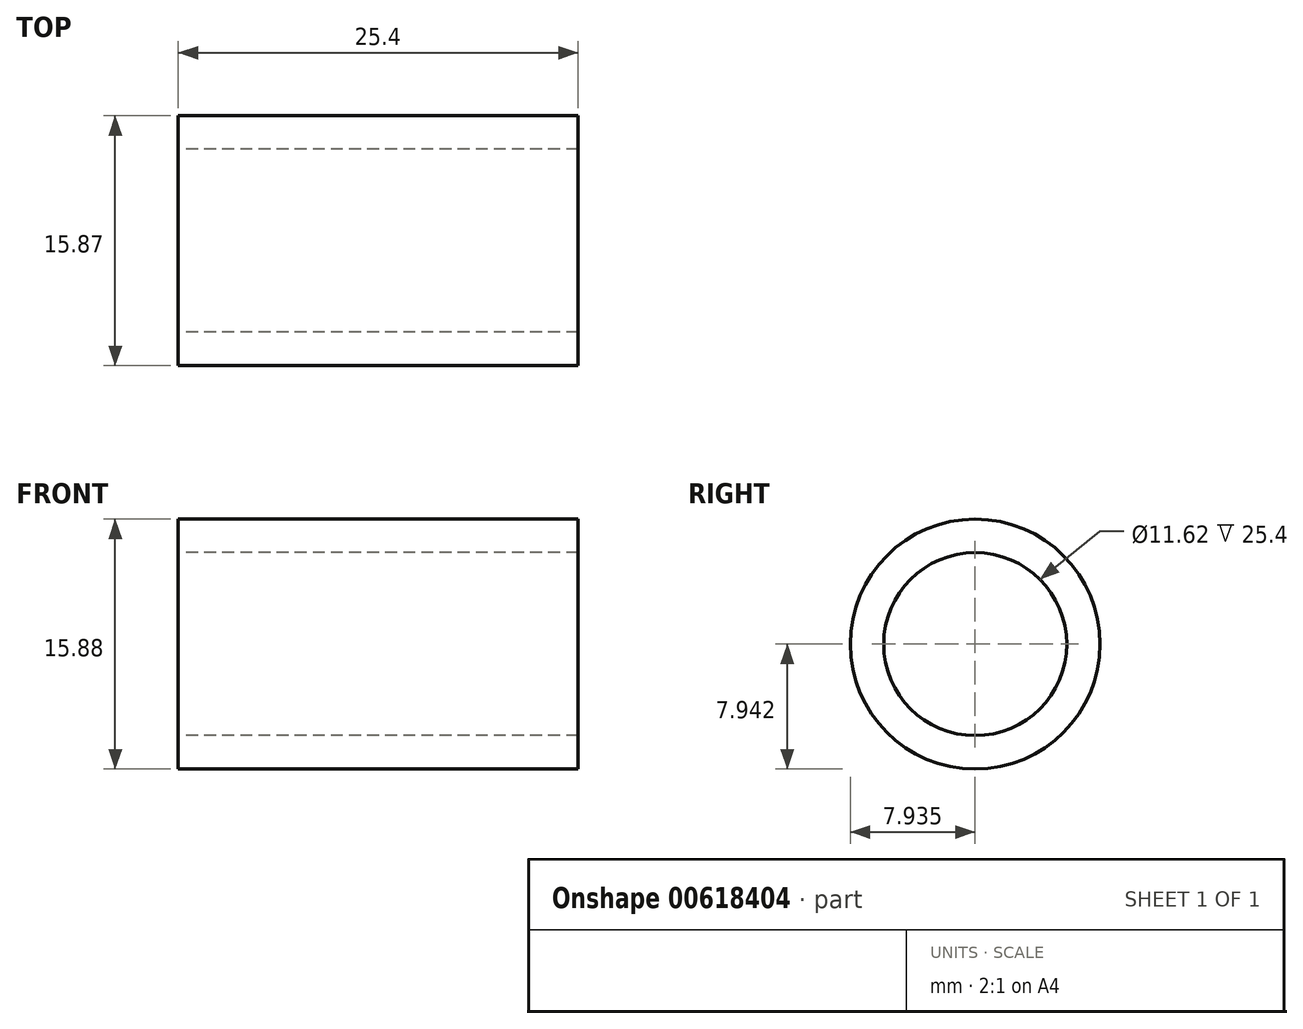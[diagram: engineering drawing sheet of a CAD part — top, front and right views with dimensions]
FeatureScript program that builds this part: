
annotation { "Feature Type Name" : "Feature", "Feature Type Description" : "" }
export const myFeature = defineFeature(function(context is Context, id is Id, definition is map)
    precondition{}
    {
        {
            var Q0;
            Q0=qCreatedBy(makeId("Right.planeOp"),FACE);
            var sketch = newSketch(context, id + "F0", { "sketchPlane" : qUnion([Q0])});
            skCircle(sketch, "E0", {"center": v(-30.8, 13.42) * mm, "radius": 7.94 * mm});
            skCircle(sketch, "E1", {"center": v(-30.8, 13.42) * mm, "radius": 5.56 * mm});
            skCircle(sketch, "E2.0", {"center": v(-30.8, 13.42) * mm, "radius": 5.81 * mm});
            skSolve(sketch);
        }
        {
            var Q0;
            Q0=makeQuery(id+"F0.imprint","IMPRINT",FACE,{"disambiguationData":[TD([[makeQuery(id+"F0.imprint","IMPRINT",EDGE,{"derivedFrom":sQuery(id+"F0.wireOp",EDGE,"E0")}),1.0]])]});
            extrude(context, id + "F1", {"entities" : qUnion([Q0]), "depth" : 25.4 * mm, "offsetDistance" : 25.4 * mm});
        }
    });
